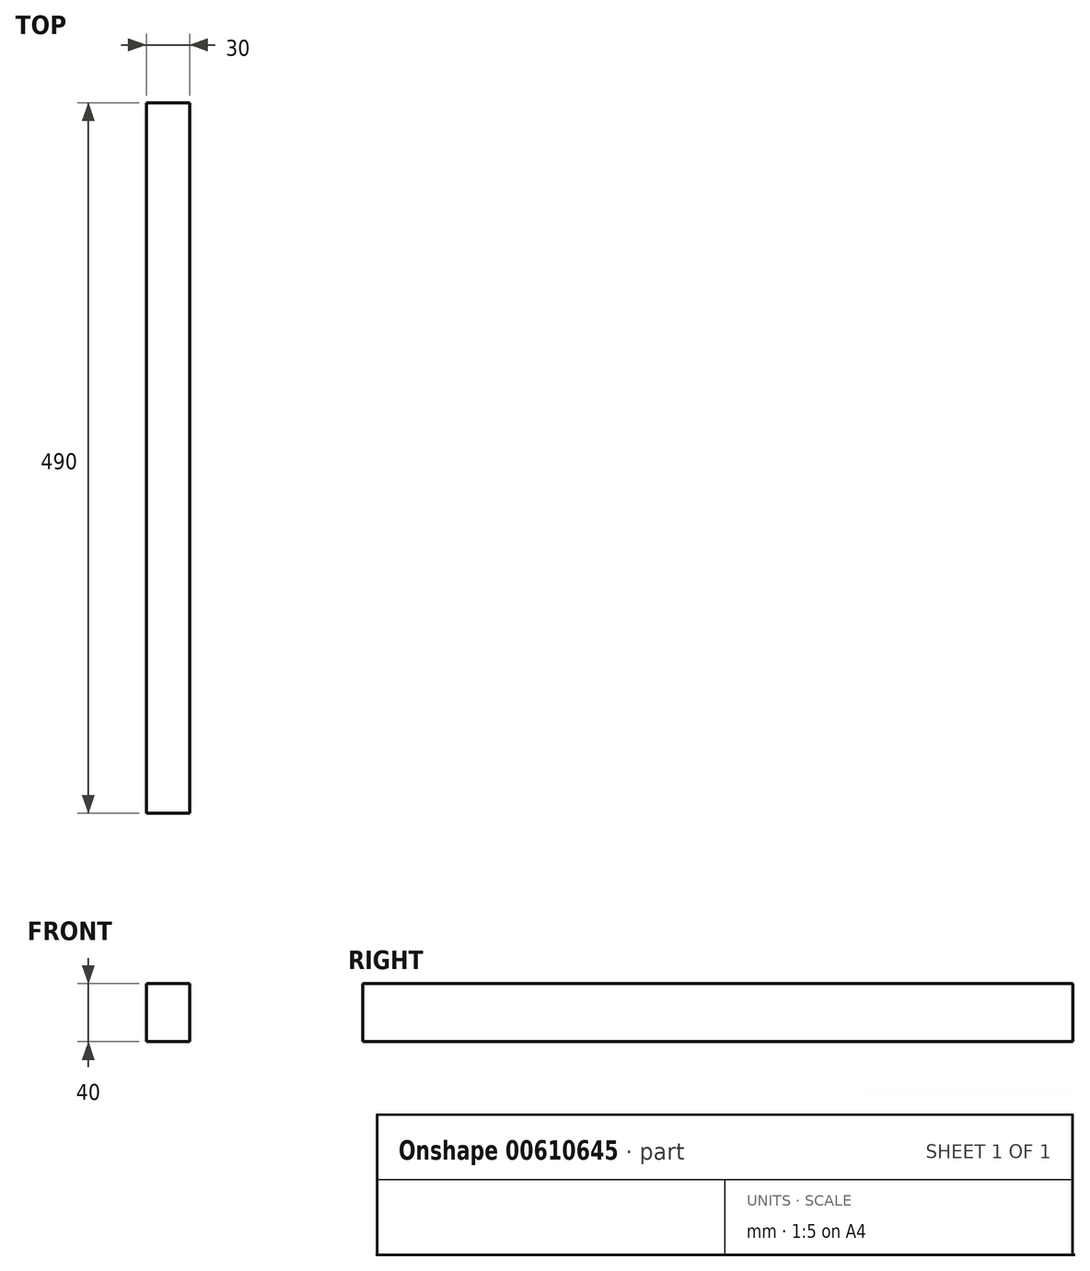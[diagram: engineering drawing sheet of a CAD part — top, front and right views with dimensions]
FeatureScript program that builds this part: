
annotation { "Feature Type Name" : "Feature", "Feature Type Description" : "" }
export const myFeature = defineFeature(function(context is Context, id is Id, definition is map)
    precondition{}
    {
        {
            var Q0;
            Q0=qCreatedBy(makeId("Right.planeOp"),FACE);
            var sketch = newSketch(context, id + "F0", { "sketchPlane" : qUnion([Q0])});
            skLineSegment(sketch, "E0.bottom", {"start": v(-59.04, -178.45) * mm, "end": v(430.96, -178.45) * mm});
            skLineSegment(sketch, "E0.top", {"start": v(-59.04, -218.45) * mm, "end": v(430.96, -218.45) * mm});
            skLineSegment(sketch, "E0.left", {"start": v(-59.04, -178.45) * mm, "end": v(-59.04, -218.45) * mm});
            skLineSegment(sketch, "E0.right", {"start": v(430.96, -178.45) * mm, "end": v(430.96, -218.45) * mm});
            skSolve(sketch);
        }
        {
            var Q0;
            Q0=qSketchRegion(id+"F0",true);
            extrude(context, id + "F1", {"entities" : qUnion([Q0]), "depth" : 30 * mm});
        }
    });
